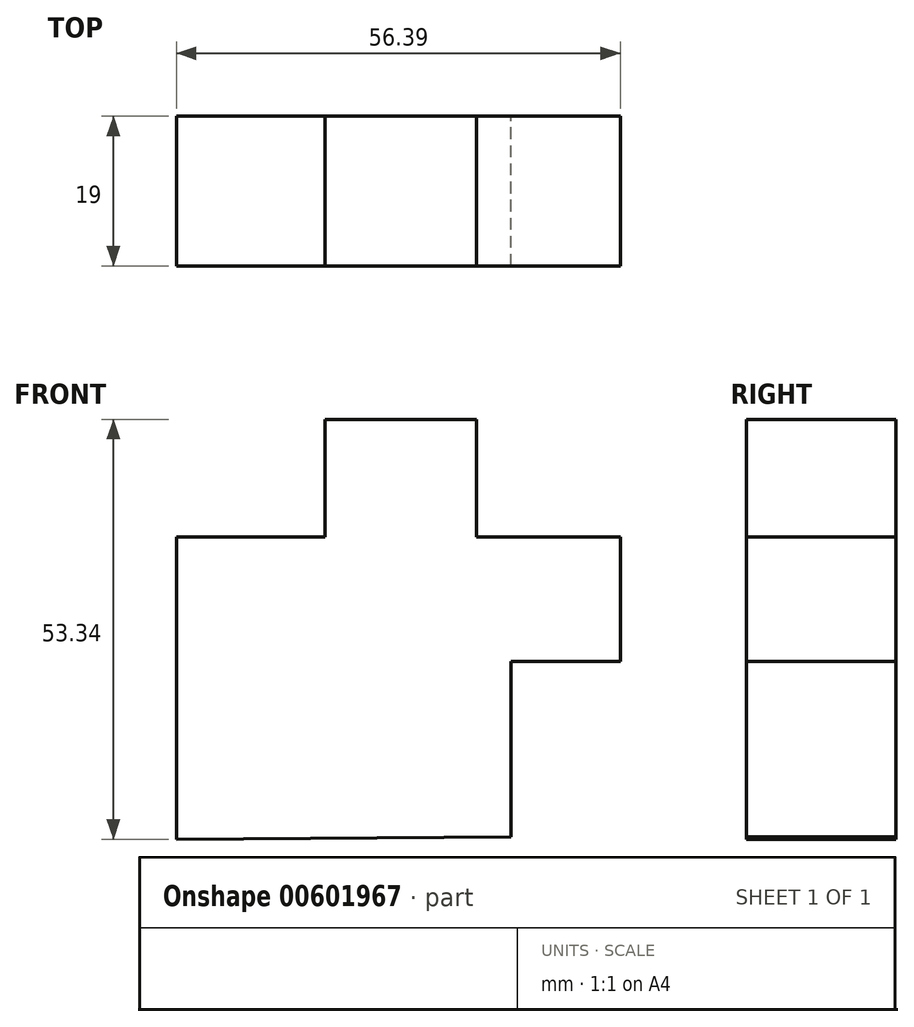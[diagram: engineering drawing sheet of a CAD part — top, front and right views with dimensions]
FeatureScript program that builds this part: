
annotation { "Feature Type Name" : "Feature", "Feature Type Description" : "" }
export const myFeature = defineFeature(function(context is Context, id is Id, definition is map)
    precondition{}
    {
        {
            var Q0;
            Q0=qCreatedBy(makeId("Front.planeOp"),FACE);
            var sketch = newSketch(context, id + "F0", { "sketchPlane" : qUnion([Q0])});
            skLineSegment(sketch, "E0", {"start": v(-42.52, 15.85) * mm, "end": v(-42.52, -22.56) * mm});
            skLineSegment(sketch, "E1", {"start": v(-42.52, 15.85) * mm, "end": v(-23.62, 15.85) * mm});
            skLineSegment(sketch, "E2", {"start": v(-23.62, 15.85) * mm, "end": v(-23.62, 30.78) * mm});
            skLineSegment(sketch, "E3", {"start": v(-23.62, 30.78) * mm, "end": v(-4.42, 30.78) * mm});
            skLineSegment(sketch, "E4", {"start": v(-4.42, 30.78) * mm, "end": v(-4.42, 15.85) * mm});
            skLineSegment(sketch, "E5", {"start": v(-4.42, 15.85) * mm, "end": v(13.87, 15.85) * mm});
            skLineSegment(sketch, "E6", {"start": v(13.87, 15.85) * mm, "end": v(13.87, 0) * mm});
            skLineSegment(sketch, "E7", {"start": v(13.87, 0) * mm, "end": v(0, 0) * mm});
            skLineSegment(sketch, "E8", {"start": v(0, 0) * mm, "end": v(0, -22.25) * mm});
            skLineSegment(sketch, "E9", {"start": v(-42.52, -22.56) * mm, "end": v(0, -22.25) * mm});
            skSolve(sketch);
        }
        {
            var Q0;
            Q0 = qSketchRegion(id + "F0", true);
            extrude(context, id + "F1", {"entities" : qUnion([Q0]), "depth" : 19 * mm, "offsetDistance" : 25.4 * mm});
        }
    });
